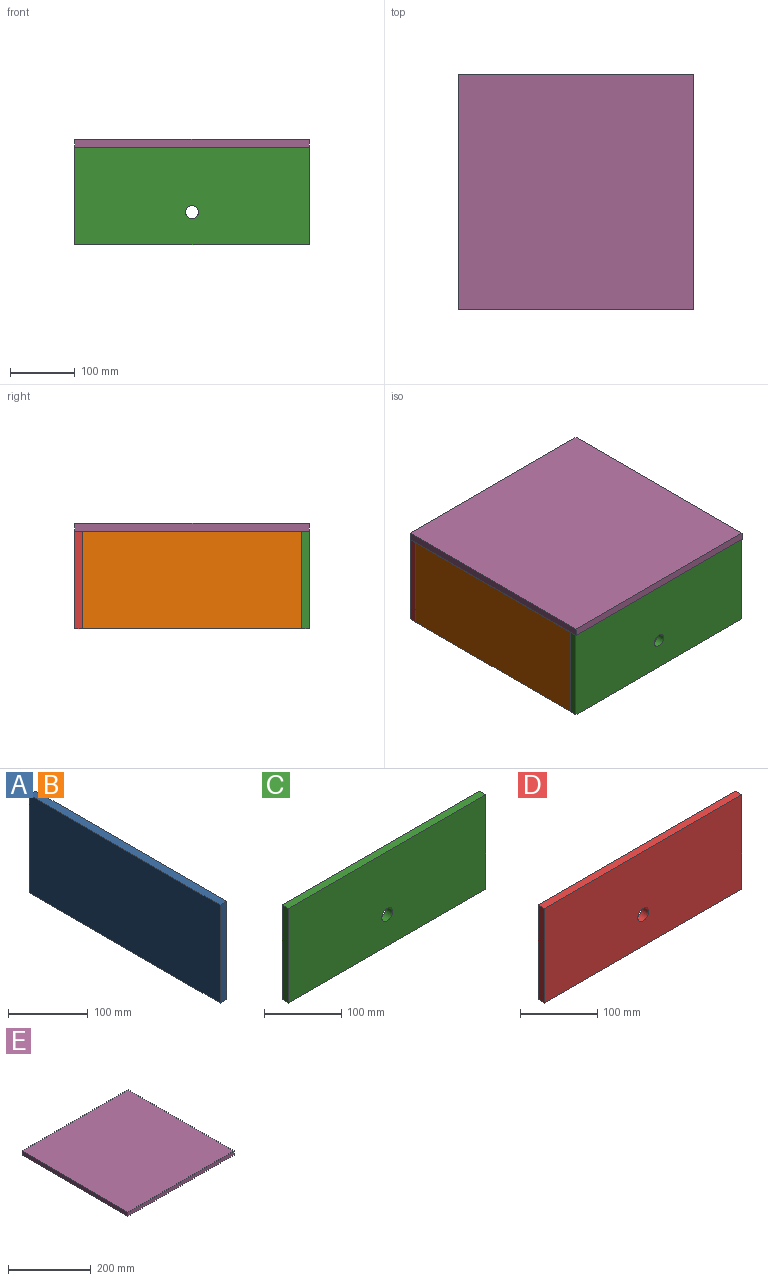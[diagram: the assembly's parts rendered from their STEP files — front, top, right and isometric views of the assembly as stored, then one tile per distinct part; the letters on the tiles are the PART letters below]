
ASSEMBLY  parts=5 mates=4
PART A: 6 faces, bbox 12x338x150 mm
  f0: plane 150x12mm, normal (0,-1,0), area 1800mm2, adj f1,f3,f4,f5
  f1: plane 338x12mm, normal (0,0,-1), area 4056mm2, adj f0,f2,f4,f5
  f2: plane 150x12mm, normal (0,1,0), area 1800mm2, adj f1,f3,f4,f5
  f3: plane 338x12mm, normal (0,0,1), area 4056mm2, adj f0,f2,f4,f5
  f4: plane 338x150mm, normal (-1,0,0), area 50700mm2, adj f0,f1,f2,f3
  f5: plane 338x150mm, normal (1,0,0), area 50700mm2, adj f0,f1,f2,f3
PART B: same geometry as A
PART C: 7 faces, bbox 362x12x150 mm
  f0: plane 150x12mm, normal (1,0,0), area 1800mm2, adj f1,f3,f4,f5
  f1: plane 362x12mm, normal (0,0,1), area 4344mm2, adj f0,f2,f4,f5
  f2: plane 150x12mm, normal (-1,0,0), area 1800mm2, adj f1,f3,f4,f5
  f3: plane 362x12mm, normal (0,0,-1), area 4344mm2, adj f0,f2,f4,f5
  f4: plane 362x150mm, normal (0,1,0), area 53985.8mm2, adj f0,f1,f2,f3,f6
  f5: plane 362x150mm, normal (0,-1,0), area 53985.8mm2, adj f0,f1,f2,f3,f6
  f6: cylinder r=10mm len=20mm, axis (0,-1,0), area 754mm2, adj f4,f5
PART D: 7 faces, bbox 362x12x150 mm
  f0: plane 150x12mm, normal (1,0,0), area 1800mm2, adj f1,f3,f4,f5
  f1: plane 362x12mm, normal (0,0,1), area 4344mm2, adj f0,f2,f4,f5
  f2: plane 150x12mm, normal (-1,0,0), area 1800mm2, adj f1,f3,f4,f5
  f3: plane 362x12mm, normal (0,0,-1), area 4344mm2, adj f0,f2,f4,f5
  f4: plane 362x150mm, normal (0,-1,0), area 53985.8mm2, adj f0,f1,f2,f3,f6
  f5: plane 362x150mm, normal (0,1,0), area 53985.8mm2, adj f0,f1,f2,f3,f6
  f6: cylinder r=10mm len=20mm, axis (0,-1,0), area 754mm2, adj f4,f5
PART E: 6 faces, bbox 362x362x12 mm
  f0: plane 362x12mm, normal (-1,0,0), area 4344mm2, adj f1,f3,f4,f5
  f1: plane 362x12mm, normal (0,-1,0), area 4344mm2, adj f0,f2,f4,f5
  f2: plane 362x12mm, normal (1,0,0), area 4344mm2, adj f1,f3,f4,f5
  f3: plane 362x12mm, normal (0,1,0), area 4344mm2, adj f0,f2,f4,f5
  f4: plane 362x362mm, normal (0,0,1), area 131044mm2, adj f0,f1,f2,f3
  f5: plane 362x362mm, normal (0,0,-1), area 131044mm2, adj f0,f1,f2,f3
PLACE A t=(-105.11,-129.78,161.98)mm
PLACE B t=(-455.11,-129.78,161.98)mm
PLACE C t=(-105.11,-129.78,161.98)mm fixed
PLACE D t=(-105.11,-129.78,161.98)mm
PLACE E t=(-104.81,-129.78,161.98)mm
MATE fastened B.f3 <-> E.f5  axis (0,0,1) through (-286.11,51.22,236.98)mm
MATE fastened E.f5 <-> D.f1  axis (0,0,-1) through (75.89,232.22,236.98)mm
MATE fastened A.f0 <-> C.f4  axis (0,-1,0) through (75.89,-117.78,86.98)mm
MATE fastened D.f4 <-> A.f2  axis (0,-1,0) through (75.89,220.22,86.98)mm
